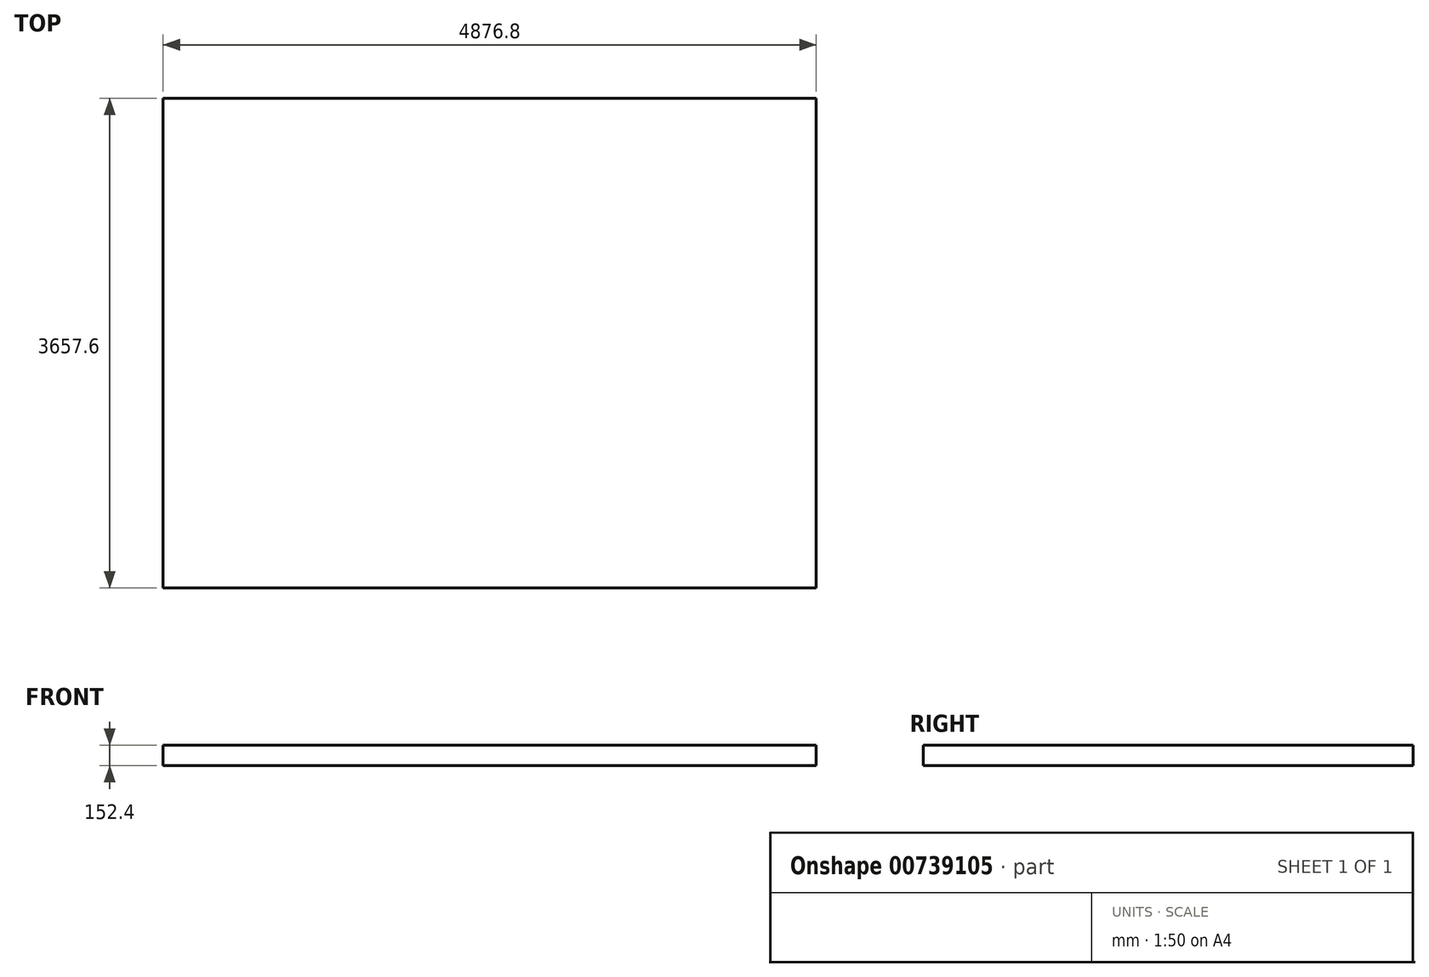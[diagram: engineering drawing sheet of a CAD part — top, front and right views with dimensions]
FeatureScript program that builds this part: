
annotation { "Feature Type Name" : "Feature", "Feature Type Description" : "" }
export const myFeature = defineFeature(function(context is Context, id is Id, definition is map)
    precondition{}
    {
        {
            var Q0;
            Q0=qCreatedBy(makeId("Top.planeOp"),FACE);
            var sketch = newSketch(context, id + "F0", { "sketchPlane" : qUnion([Q0])});
            skLineSegment(sketch, "E0.bottom", {"start": v(0, 3657.6) * mm, "end": v(4876.8, 3657.6) * mm});
            skLineSegment(sketch, "E0.top", {"start": v(0, 0) * mm, "end": v(4876.8, 0) * mm});
            skLineSegment(sketch, "E0.left", {"start": v(0, 3657.6) * mm, "end": v(0, 0) * mm});
            skLineSegment(sketch, "E0.right", {"start": v(4876.8, 3657.6) * mm, "end": v(4876.8, 0) * mm});
            skSolve(sketch);
        }
        {
            var Q0;
            Q0 = qSketchRegion(id + "F0", true);
            extrude(context, id + "F1", {"entities" : qUnion([Q0]), "oppositeDirection" : true, "depth" : 152.4 * mm, "offsetDistance" : 25.4 * mm});
        }
    });
